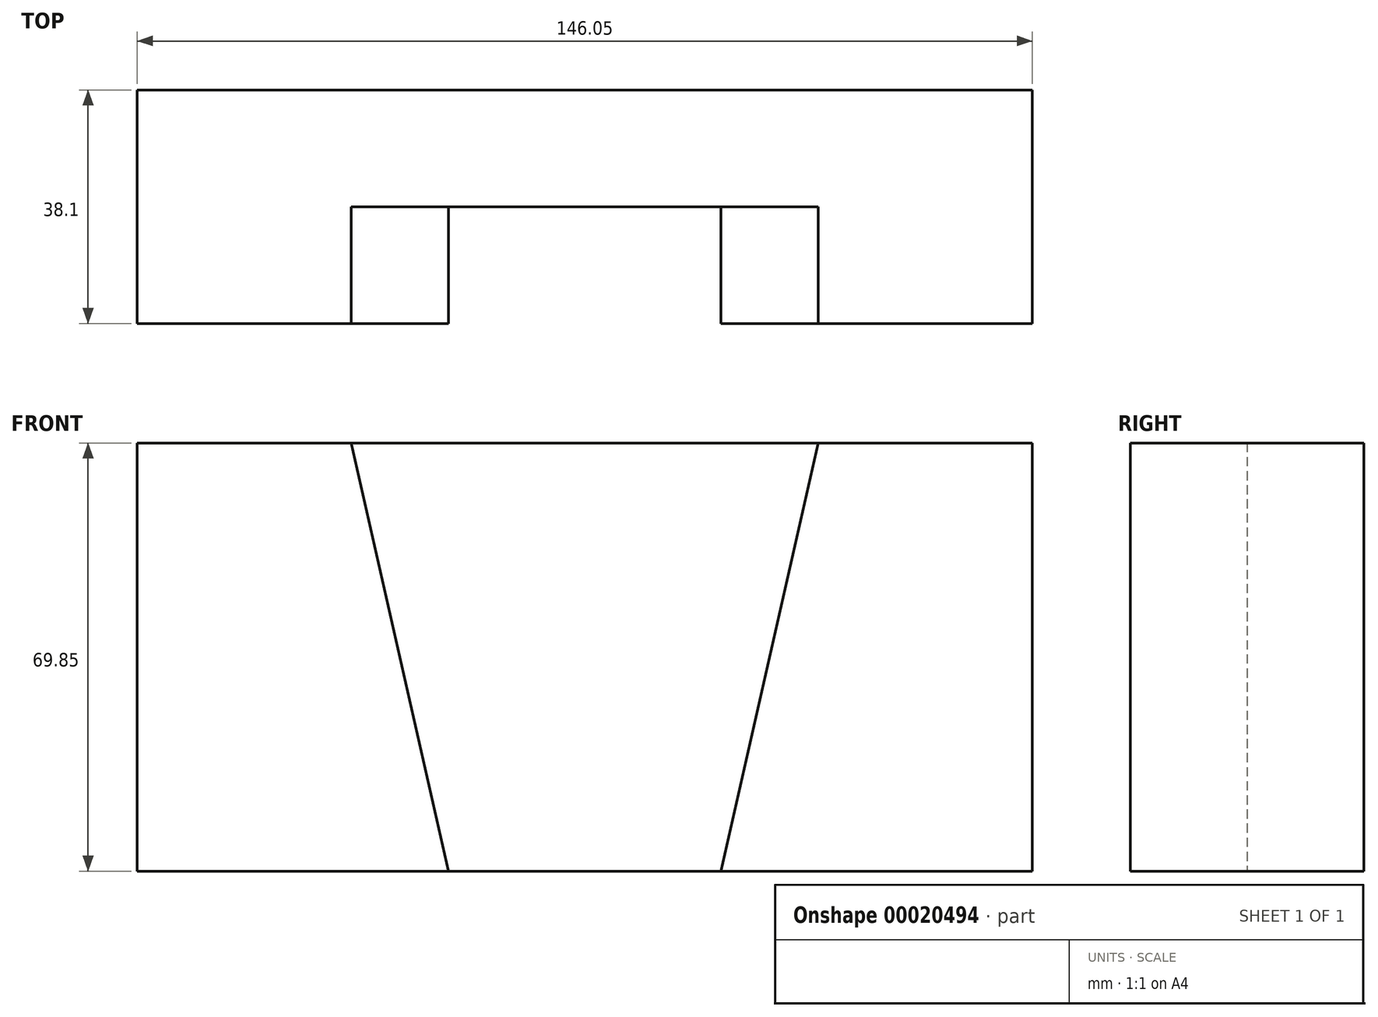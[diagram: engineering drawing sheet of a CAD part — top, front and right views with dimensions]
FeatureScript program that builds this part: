
annotation { "Feature Type Name" : "Feature", "Feature Type Description" : "" }
export const myFeature = defineFeature(function(context is Context, id is Id, definition is map)
    precondition{}
    {
        {
            var Q0;
            Q0=qCreatedBy(makeId("Front.planeOp"),FACE);
            var sketch = newSketch(context, id + "F0", { "sketchPlane" : qUnion([Q0])});
            skLineSegment(sketch, "E0.bottom", {"start": v(-81.37, -30.98) * mm, "end": v(64.68, -30.98) * mm});
            skLineSegment(sketch, "E0.top", {"start": v(-81.37, 38.87) * mm, "end": v(64.68, 38.87) * mm});
            skLineSegment(sketch, "E0.left", {"start": v(-81.37, -30.98) * mm, "end": v(-81.37, 38.87) * mm});
            skLineSegment(sketch, "E0.right", {"start": v(64.68, -30.98) * mm, "end": v(64.68, 38.87) * mm});
            skPoint(sketch, "E1", {"position": v(-30.57, -30.98) * mm});
            skPoint(sketch, "E2", {"position": v(13.88, -30.98) * mm});
            skPoint(sketch, "E3", {"position": v(-46.44, 38.87) * mm});
            skPoint(sketch, "E4", {"position": v(29.76, 38.87) * mm});
            skLineSegment(sketch, "E5", {"start": v(13.88, -30.98) * mm, "end": v(29.76, 38.87) * mm});
            skLineSegment(sketch, "E6", {"start": v(-46.44, 38.87) * mm, "end": v(-30.57, -30.98) * mm});
            skSolve(sketch);
        }
        {
            var Q0;
            {var subQ1=sQuery(id+"F0.wireOp",EDGE,"E5");Q0=makeQuery(id+"F0.imprint","IMPRINT",FACE,{"disambiguationData":[TD([[makeQuery(id+"F0.imprint","IMPRINT",EDGE,{"derivedFrom":subQ1}),1.0]])]});}
            extrude(context, id + "F1", {"entities" : qUnion([Q0]), "depth" : 19.05 * mm});
        }
        {
            var Q0;
            {var subQ1=sQuery(id+"F0.wireOp",EDGE,"E0.right");Q0=makeQuery(id+"F0.imprint","IMPRINT",FACE,{"disambiguationData":[TD([[makeQuery(id+"F0.imprint","IMPRINT",EDGE,{"derivedFrom":subQ1}),1.0]])]});}
            extrude(context, id + "F2", {"entities" : qUnion([Q0]), "operationType" : NewBodyOperationType.ADD, "depth" : 38.1 * mm});
        }
        {
            var Q0;
            {var subQ1=sQuery(id+"F0.wireOp",EDGE,"E0.left");Q0=makeQuery(id+"F0.imprint","IMPRINT",FACE,{"disambiguationData":[TD([[makeQuery(id+"F0.imprint","IMPRINT",EDGE,{"derivedFrom":subQ1}),-1.0]])]});}
            extrude(context, id + "F3", {"entities" : qUnion([Q0]), "operationType" : NewBodyOperationType.ADD, "depth" : 38.1 * mm});
        }
    });
